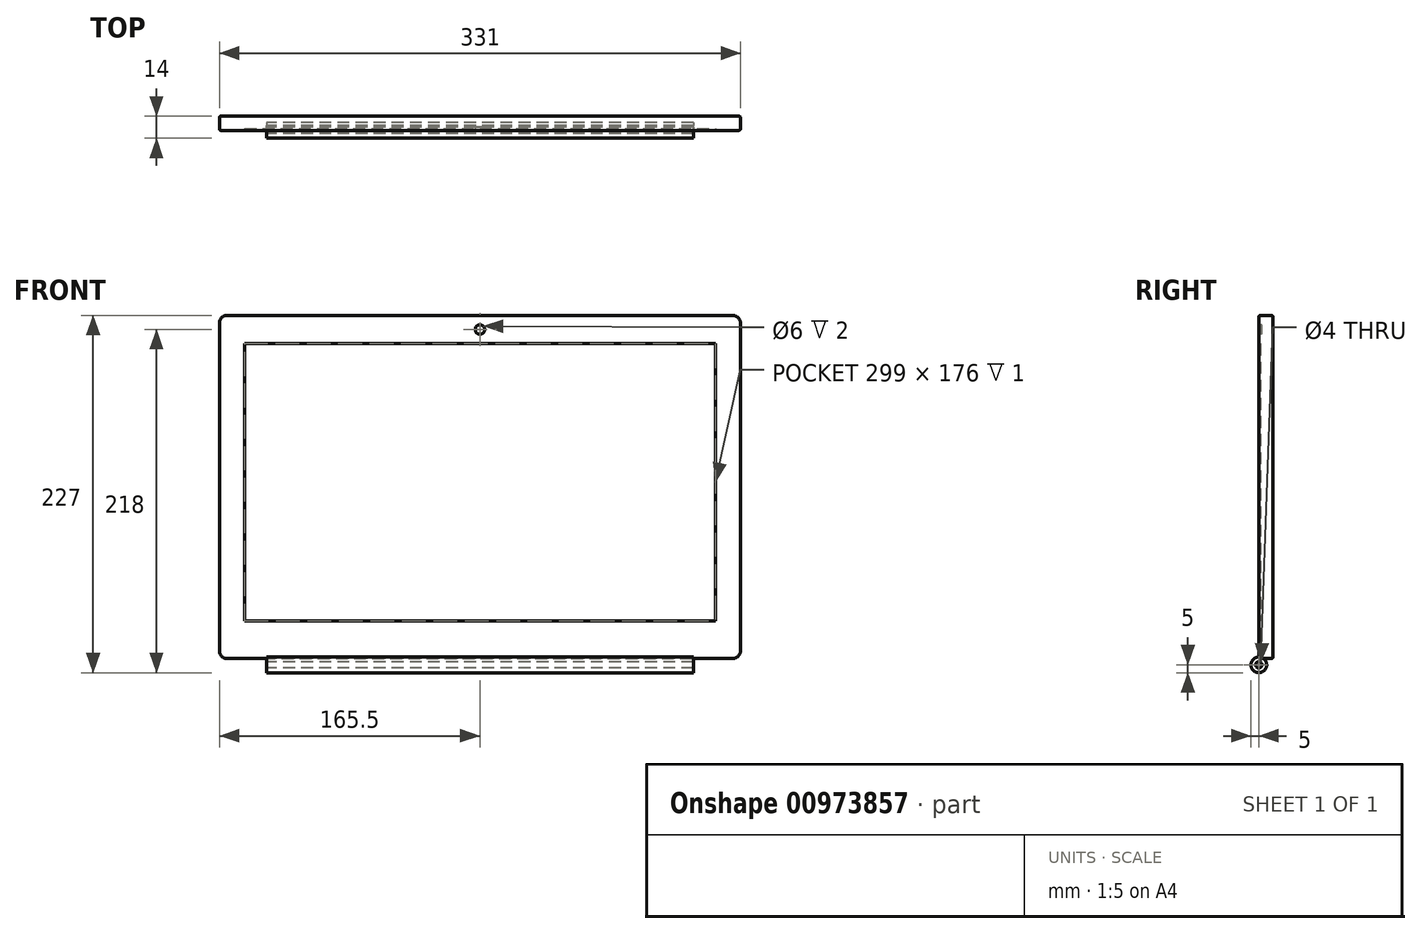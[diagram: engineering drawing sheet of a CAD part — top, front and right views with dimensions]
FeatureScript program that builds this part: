
annotation { "Feature Type Name" : "Feature", "Feature Type Description" : "" }
export const myFeature = defineFeature(function(context is Context, id is Id, definition is map)
    precondition{}
    {
        {
            var Q0;
            Q0=qCreatedBy(makeId("Front.planeOp"),FACE);
            var sketch = newSketch(context, id + "F0", { "sketchPlane" : qUnion([Q0])});
            skLineSegment(sketch, "E0.bottom", {"start": v(-165.5, 218) * mm, "end": v(165.5, 218) * mm});
            skLineSegment(sketch, "E0.top", {"start": v(-165.5, 0) * mm, "end": v(165.5, 0) * mm});
            skLineSegment(sketch, "E0.left", {"start": v(-165.5, 218) * mm, "end": v(-165.5, 0) * mm});
            skLineSegment(sketch, "E0.right", {"start": v(165.5, 218) * mm, "end": v(165.5, 0) * mm});
            skSolve(sketch);
        }
        {
            var Q0;
            Q0=makeQuery(id+"F0.imprint","IMPRINT",FACE,{"disambiguationData":[TD([[makeQuery(id+"F0.imprint","IMPRINT",EDGE,{"derivedFrom":sQuery(id+"F0.wireOp",EDGE,"E0.bottom")}),-1.0]])]});
            extrude(context, id + "F1", {"entities" : qUnion([Q0]), "depth" : 9 * mm, "offsetDistance" : 25 * mm});
        }
        {
            var Q0;
            Q0=makeQuery(id+"F1.opExtrude","CAP_FACE",FACE,{"disambiguationData":[OSD([sQuery(id+"F0.wireOp",EDGE,"E0.bottom"),sQuery(id+"F0.wireOp",EDGE,"E0.top"),sQuery(id+"F0.wireOp",EDGE,"E0.left"),sQuery(id+"F0.wireOp",EDGE,"E0.right")])],"isStart":false});
            var sketch = newSketch(context, id + "F2", { "sketchPlane" : qUnion([Q0])});
            skLineSegment(sketch, "E1.bottom", {"start": v(-149.5, 200) * mm, "end": v(149.5, 200) * mm});
            skLineSegment(sketch, "E1.top", {"start": v(-149.5, 24) * mm, "end": v(149.5, 24) * mm});
            skLineSegment(sketch, "E1.left", {"start": v(-149.5, 200) * mm, "end": v(-149.5, 24) * mm});
            skLineSegment(sketch, "E1.right", {"start": v(149.5, 200) * mm, "end": v(149.5, 24) * mm});
            skLineSegment(sketch, "E2", {"start": v(0, 24) * mm, "end": v(0, 0) * mm, "construction": true});
            skSolve(sketch);
        }
        {
            var Q0;
            Q0=qSketchRegion(id+"F2",true);
            extrude(context, id + "F3", {"entities" : qUnion([Q0]), "operationType" : NewBodyOperationType.REMOVE, "oppositeDirection" : true, "depth" : 1 * mm, "offsetDistance" : 25 * mm});
        }
        {
            var Q0;
            Q0=makeQuery(id+"F1.opExtrude","CAP_FACE",FACE,{"disambiguationData":[OSD([sQuery(id+"F0.wireOp",EDGE,"E0.bottom"),sQuery(id+"F0.wireOp",EDGE,"E0.top"),sQuery(id+"F0.wireOp",EDGE,"E0.left"),sQuery(id+"F0.wireOp",EDGE,"E0.right")])],"isStart":false});
            var sketch = newSketch(context, id + "F4", { "sketchPlane" : qUnion([Q0])});
            skCircle(sketch, "E3", {"center": v(0, 209) * mm, "radius": 3 * mm});
            skLineSegment(sketch, "E4", {"start": v(0, 218) * mm, "end": v(0, 209) * mm, "construction": true});
            skLineSegment(sketch, "E5", {"start": v(0, 209) * mm, "end": v(0, 200) * mm, "construction": true});
            skLineSegment(sketch, "E6", {"start": v(0, 200) * mm, "end": v(0, 0) * mm, "construction": true});
            skSolve(sketch);
        }
        {
            var Q0;
            Q0=qSketchRegion(id+"F4",true);
            extrude(context, id + "F5", {"entities" : qUnion([Q0]), "operationType" : NewBodyOperationType.REMOVE, "oppositeDirection" : true, "depth" : 2 * mm, "offsetDistance" : 25 * mm});
        }
        {
            var Q0;
            Q0=qCreatedBy(makeId("Right.planeOp"),FACE);
            var sketch = newSketch(context, id + "F6", { "sketchPlane" : qUnion([Q0])});
            skCircle(sketch, "E7", {"center": v(-9, -4) * mm, "radius": 5 * mm});
            skCircle(sketch, "E8", {"center": v(-9, -4) * mm, "radius": 2 * mm});
            skLineSegment(sketch, "E9", {"start": v(-9, -4) * mm, "end": v(-9, 0) * mm, "construction": true});
            skSolve(sketch);
        }
        {
            var Q0;
            Q0=qSketchRegion(id+"F6",true);
            extrude(context, id + "F7", {"entities" : qUnion([Q0]), "operationType" : NewBodyOperationType.ADD, "endBound" : BoundingType.SYMMETRIC, "depth" : 271 * mm, "offsetDistance" : 25 * mm});
        }
        {
            var Q0;
            Q0=makeQuery(id+"F1.opExtrude","SWEPT_EDGE",EDGE,{"disambiguationData":[OSD([sQuery(id+"F0.wireOp",EDGE,"E0.top"),sQuery(id+"F0.wireOp",EDGE,"E0.right")])]});
            var Q1;
            Q1=makeQuery(id+"F1.opExtrude","SWEPT_EDGE",EDGE,{"disambiguationData":[OSD([sQuery(id+"F0.wireOp",EDGE,"E0.bottom"),sQuery(id+"F0.wireOp",EDGE,"E0.right")])]});
            var Q2;
            Q2=makeQuery(id+"F1.opExtrude","SWEPT_EDGE",EDGE,{"disambiguationData":[OSD([sQuery(id+"F0.wireOp",EDGE,"E0.bottom"),sQuery(id+"F0.wireOp",EDGE,"E0.left")])]});
            var Q3;
            Q3=makeQuery(id+"F1.opExtrude","SWEPT_EDGE",EDGE,{"disambiguationData":[OSD([sQuery(id+"F0.wireOp",EDGE,"E0.top"),sQuery(id+"F0.wireOp",EDGE,"E0.left")])]});
            fillet(context, id + "F8", {"entities" : qUnion([Q0, Q1, Q2, Q3]), "radius" : 5 * mm, "tangentPropagation" : true, "allowEdgeOverflow" : false});
        }
        {
            var Q0;
            Q0=makeQuery(id+"F1.opExtrude","CAP_EDGE",EDGE,{"disambiguationData":[OSD([sQuery(id+"F0.wireOp",EDGE,"E0.left")])],"isStart":false});
            var Q1;
            Q1=makeQuery(id+"F1.opExtrude","CAP_EDGE",EDGE,{"disambiguationData":[OSD([sQuery(id+"F0.wireOp",EDGE,"E0.left")])],"isStart":true});
            fillet(context, id + "F9", {"entities" : qUnion([Q0, Q1]), "radius" : 1 * mm, "tangentPropagation" : true, "allowEdgeOverflow" : false});
        }
    });
